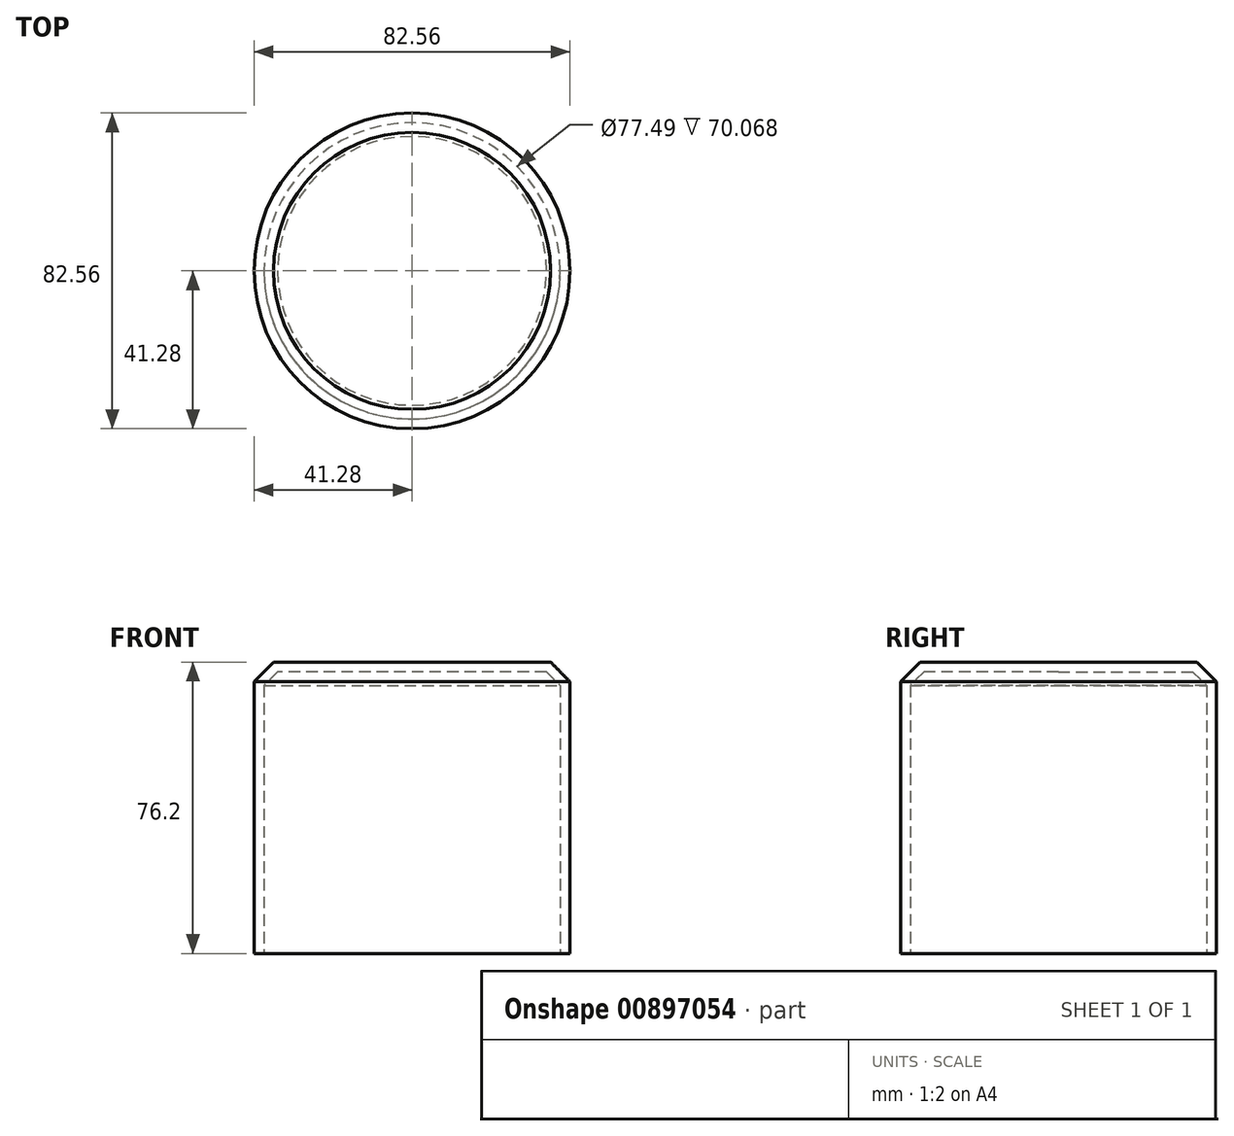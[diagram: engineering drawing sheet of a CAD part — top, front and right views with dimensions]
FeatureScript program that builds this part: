
annotation { "Feature Type Name" : "Feature", "Feature Type Description" : "" }
export const myFeature = defineFeature(function(context is Context, id is Id, definition is map)
    precondition{}
    {
        {
            var Q0;
            Q0=qCreatedBy(makeId("Top.planeOp"),FACE);
            var sketch = newSketch(context, id + "F0", { "sketchPlane" : qUnion([Q0])});
            skCircle(sketch, "E0", {"center": v(0, 0) * mm, "radius": 41.28 * mm});
            skSolve(sketch);
        }
        {
            var Q0;
            Q0 = qSketchRegion(id + "F0", true);
            extrude(context, id + "F1", {"entities" : qUnion([Q0]), "depth" : 76.2 * mm, "offsetDistance" : 25.4 * mm});
        }
        {
            var Q0;
            Q0=makeQuery(id+"F1.opExtrude","CAP_EDGE",EDGE,{"disambiguationData":[OSD([sQuery(id+"F0.wireOp",EDGE,"E0")])],"isStart":false});
            chamfer(context, id + "F2", {"entities" : qUnion([Q0]), "width" : 5.08 * mm, "tangentPropagation" : true});
        }
        {
            var Q0;
            Q0=makeQuery(id+"F1.opExtrude","CAP_FACE",FACE,{"disambiguationData":[OSD([sQuery(id+"F0.wireOp",EDGE,"E0")])],"isStart":true});
            shell(context, id + "F3", {"entities" : qUnion([Q0]), "thickness" : 2.54 * mm});
        }
    });
